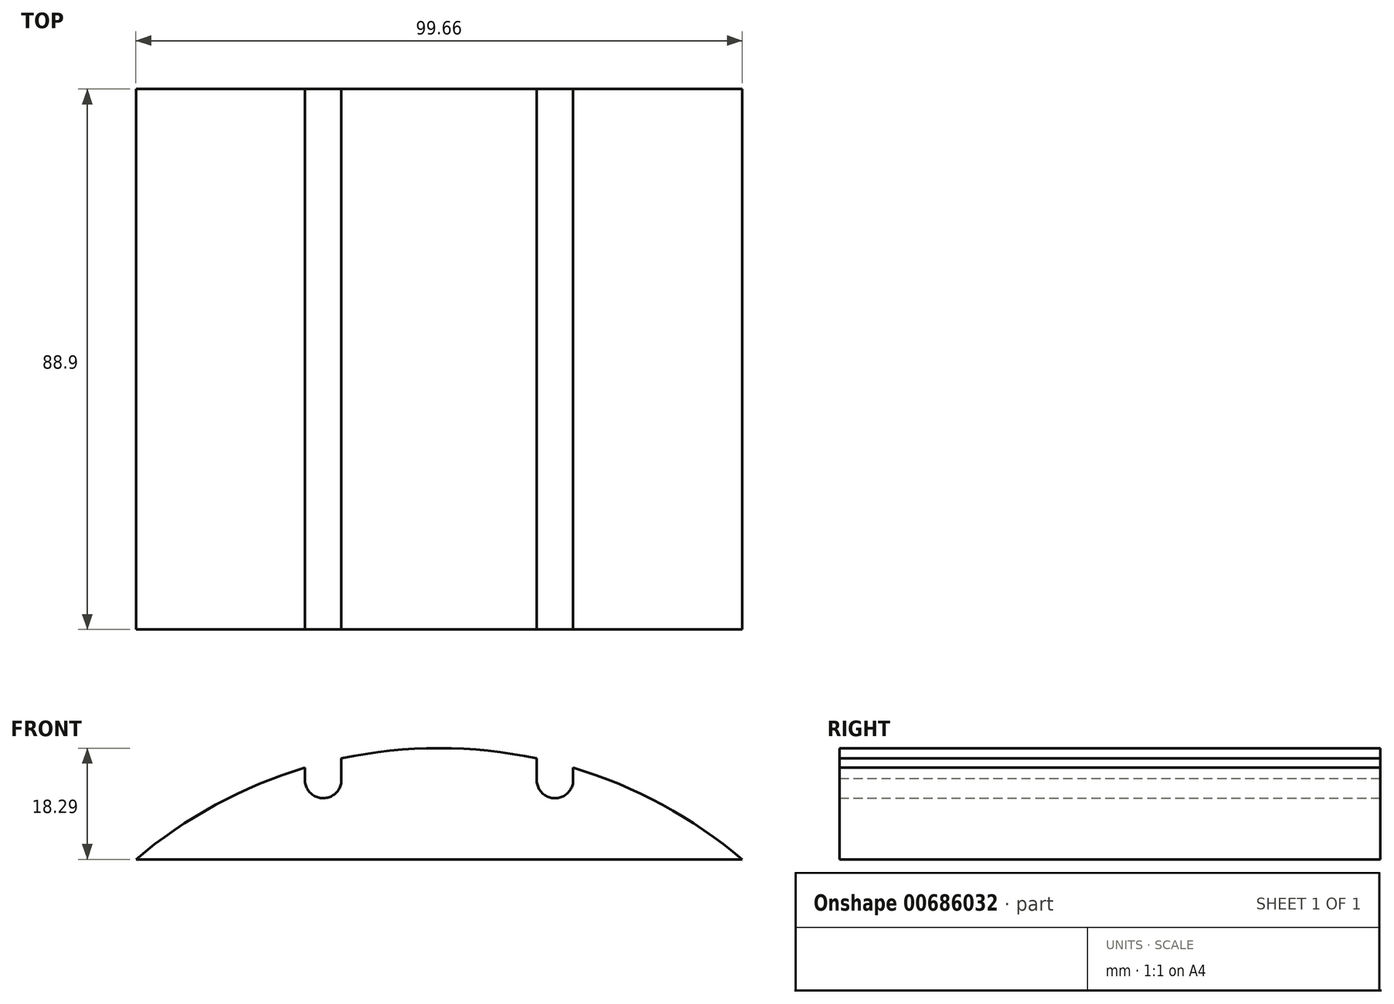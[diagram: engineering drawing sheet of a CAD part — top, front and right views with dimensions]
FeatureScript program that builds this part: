
annotation { "Feature Type Name" : "Feature", "Feature Type Description" : "" }
export const myFeature = defineFeature(function(context is Context, id is Id, definition is map)
    precondition{}
    {
        {
            var Q0;
            Q0=qCreatedBy(makeId("Front.planeOp"),FACE);
            var sketch = newSketch(context, id + "F0", { "sketchPlane" : qUnion([Q0])});
            skCircle(sketch, "E0", {"center": v(0, 0) * mm, "radius": 77.03 * mm});
            skLineSegment(sketch, "E1.bottom", {"start": v(-75.18, 58.74) * mm, "end": v(75.18, 58.74) * mm});
            skLineSegment(sketch, "E1.top", {"start": v(-75.18, -62.22) * mm, "end": v(75.18, -62.22) * mm});
            skLineSegment(sketch, "E1.left", {"start": v(-75.18, 58.74) * mm, "end": v(-75.18, -62.22) * mm});
            skLineSegment(sketch, "E1.right", {"start": v(75.18, 58.74) * mm, "end": v(75.18, -62.22) * mm});
            skCircle(sketch, "E2", {"center": v(-19.05, 71.8) * mm, "radius": 3 * mm});
            skCircle(sketch, "E3", {"center": v(19.05, 71.8) * mm, "radius": 3 * mm});
            skLineSegment(sketch, "E4.bottom", {"start": v(-22.05, 71.8) * mm, "end": v(-16.06, 71.8) * mm});
            skLineSegment(sketch, "E4.top", {"start": v(-22.05, 77.92) * mm, "end": v(-16.06, 77.92) * mm});
            skLineSegment(sketch, "E4.left", {"start": v(-22.05, 71.8) * mm, "end": v(-22.05, 77.92) * mm});
            skLineSegment(sketch, "E4.right", {"start": v(-16.06, 71.8) * mm, "end": v(-16.06, 77.92) * mm});
            skLineSegment(sketch, "E5.bottom", {"start": v(22.05, 71.8) * mm, "end": v(16.06, 71.8) * mm});
            skLineSegment(sketch, "E5.top", {"start": v(22.05, 78.56) * mm, "end": v(16.06, 78.56) * mm});
            skLineSegment(sketch, "E5.left", {"start": v(22.05, 71.8) * mm, "end": v(22.05, 78.56) * mm});
            skLineSegment(sketch, "E5.right", {"start": v(16.06, 71.8) * mm, "end": v(16.06, 78.56) * mm});
            skLineSegment(sketch, "E6.bottom", {"start": v(-50.8, 46.04) * mm, "end": v(50.8, 46.04) * mm});
            skLineSegment(sketch, "E6.top", {"start": v(-50.8, 39.69) * mm, "end": v(50.8, 39.69) * mm});
            skLineSegment(sketch, "E6.left", {"start": v(-50.8, 46.04) * mm, "end": v(-50.8, 39.69) * mm});
            skLineSegment(sketch, "E6.right", {"start": v(50.8, 46.04) * mm, "end": v(50.8, 39.69) * mm});
            skLineSegment(sketch, "E7.bottom", {"start": v(-46.05, 50.8) * mm, "end": v(-39.7, 50.8) * mm});
            skLineSegment(sketch, "E7.top", {"start": v(-46.05, -50.8) * mm, "end": v(-39.7, -50.8) * mm});
            skLineSegment(sketch, "E7.left", {"start": v(-46.05, 50.8) * mm, "end": v(-46.05, -50.8) * mm});
            skLineSegment(sketch, "E7.right", {"start": v(-39.7, 50.8) * mm, "end": v(-39.7, -50.8) * mm});
            skPoint(sketch, "E8", {"position": v(-49.83, 58.74) * mm});
            skPoint(sketch, "E9", {"position": v(49.83, 58.74) * mm});
            skSolve(sketch);
        }
        {
            var Q0;
            {var subQ1=sQuery(id+"F0.wireOp",EDGE,"E0");var subQ12=sQuery(id+"F0.wireOp",EDGE,"E5.left");var subQ15=makeQuery(id+"F0.imprint","INTERSECT",VERTEX,{"derivedFrom":[subQ1,subQ12]});Q0=makeQuery(id+"F0.imprint","IMPRINT",FACE,{"disambiguationData":[TD([[makeQuery(id+"F0.imprint","IMPRINT",EDGE,{"disambiguationData":[TD([[subQ15,1.0]])],"derivedFrom":subQ1}),1.0]])]});}
            extrude(context, id + "F1", {"entities" : qUnion([Q0]), "depth" : 88.9 * mm, "offsetDistance" : 25.4 * mm});
        }
    });
